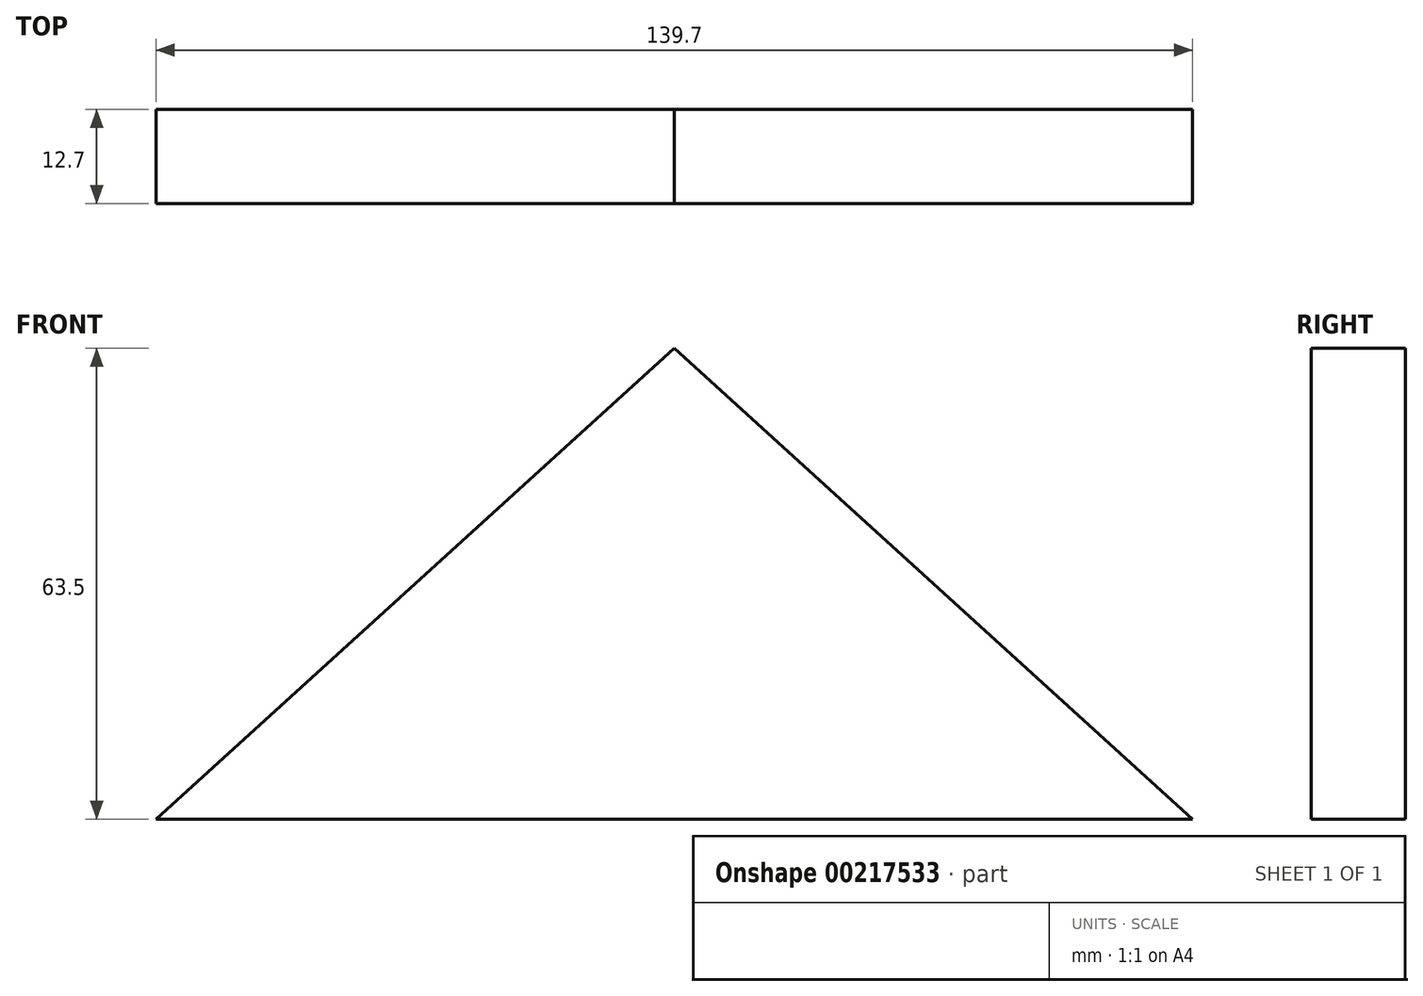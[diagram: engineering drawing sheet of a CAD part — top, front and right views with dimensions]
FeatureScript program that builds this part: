
annotation { "Feature Type Name" : "Feature", "Feature Type Description" : "" }
export const myFeature = defineFeature(function(context is Context, id is Id, definition is map)
    precondition{}
    {
        {
            var Q0;
            Q0=qCreatedBy(makeId("Front.planeOp"),FACE);
            var sketch = newSketch(context, id + "F0", { "sketchPlane" : qUnion([Q0])});
            skLineSegment(sketch, "E0", {"start": v(0, 0) * mm, "end": v(-69.85, -63.5) * mm});
            skLineSegment(sketch, "E1", {"start": v(-69.85, -63.5) * mm, "end": v(69.85, -63.5) * mm});
            skLineSegment(sketch, "E2", {"start": v(69.85, -63.5) * mm, "end": v(0, 0) * mm});
            skSolve(sketch);
        }
        {
            var Q0;
            Q0 = qSketchRegion(id + "F0", true);
            extrude(context, id + "F1", {"entities" : qUnion([Q0]), "depth" : 12.7 * mm});
        }
    });
